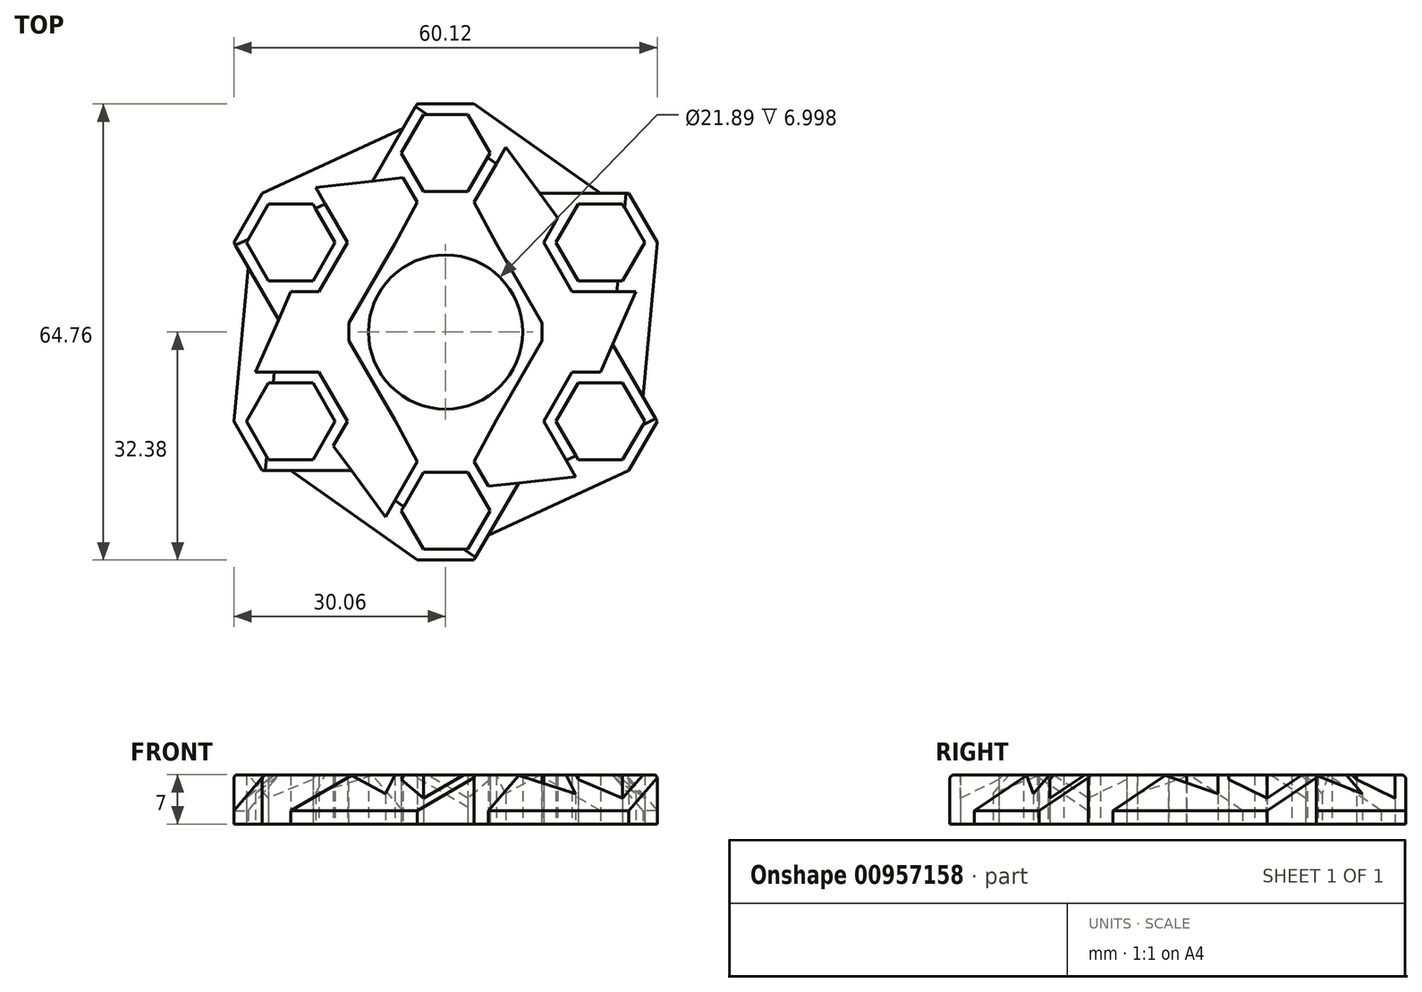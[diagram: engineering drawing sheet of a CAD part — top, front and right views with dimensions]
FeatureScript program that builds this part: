
annotation { "Feature Type Name" : "Feature", "Feature Type Description" : "" }
export const myFeature = defineFeature(function(context is Context, id is Id, definition is map)
    precondition{}
    {
        {
            var Q0;
            Q0=qCreatedBy(makeId("Top.planeOp"),FACE);
            var sketch = newSketch(context, id + "F0", { "sketchPlane" : qUnion([Q0])});
            skCircle(sketch, "E0", {"center": v(0, 0) * mm, "radius": 10.95 * mm});
            skCircle(sketch, "E1.cCircle", {"center": v(0, 0) * mm, "radius": 12.5 * mm, "construction": true});
            skLineSegment(sketch, "E1.0", {"start": v(-7.22, 12.5) * mm, "end": v(7.22, 12.5) * mm});
            skLineSegment(sketch, "E1.1", {"start": v(7.22, 12.5) * mm, "end": v(14.44, 0) * mm});
            skLineSegment(sketch, "E1.2", {"start": v(14.44, 0) * mm, "end": v(7.22, -12.5) * mm});
            skLineSegment(sketch, "E1.3", {"start": v(7.22, -12.5) * mm, "end": v(-7.22, -12.5) * mm});
            skLineSegment(sketch, "E1.4", {"start": v(-7.22, -12.5) * mm, "end": v(-14.44, 0) * mm});
            skLineSegment(sketch, "E1.5", {"start": v(-14.44, 0) * mm, "end": v(-7.22, 12.5) * mm});
            skPoint(sketch, "E1.0.midPoint", {"position": v(0, 12.5) * mm});
            skLineSegment(sketch, "E2", {"start": v(0, 0) * mm, "end": v(-2.16, 1.25) * mm});
            skLineSegment(sketch, "E3", {"start": v(0, 0) * mm, "end": v(22, -12.7) * mm});
            skLineSegment(sketch, "E4", {"start": v(22, -12.7) * mm, "end": v(-22, 12.7) * mm});
            skLineSegment(sketch, "E5", {"start": v(0, 0) * mm, "end": v(-22, -12.7) * mm});
            skLineSegment(sketch, "E6", {"start": v(0, 0) * mm, "end": v(22, 12.7) * mm});
            skCircle(sketch, "E7.cCircle", {"center": v(0, 25.4) * mm, "radius": 6.99 * mm, "construction": true});
            skLineSegment(sketch, "E7.0", {"start": v(4.03, 18.41) * mm, "end": v(-4.03, 18.41) * mm});
            skLineSegment(sketch, "E7.1", {"start": v(-4.03, 18.42) * mm, "end": v(-8.07, 25.4) * mm});
            skLineSegment(sketch, "E7.2", {"start": v(-8.07, 25.4) * mm, "end": v(-4.03, 32.39) * mm});
            skLineSegment(sketch, "E7.3", {"start": v(-4.03, 32.38) * mm, "end": v(4.03, 32.38) * mm});
            skLineSegment(sketch, "E7.4", {"start": v(4.03, 32.39) * mm, "end": v(8.07, 25.4) * mm});
            skLineSegment(sketch, "E7.5", {"start": v(8.07, 25.4) * mm, "end": v(4.03, 18.42) * mm});
            skPoint(sketch, "E7.0.midPoint", {"position": v(0, 18.41) * mm});
            skCircle(sketch, "E8.cCircle", {"center": v(22, 12.7) * mm, "radius": 6.98 * mm, "construction": true});
            skLineSegment(sketch, "E8.0", {"start": v(17.96, 5.71) * mm, "end": v(13.93, 12.7) * mm});
            skLineSegment(sketch, "E8.1", {"start": v(13.93, 12.7) * mm, "end": v(17.96, 19.68) * mm});
            skLineSegment(sketch, "E8.2", {"start": v(17.96, 19.68) * mm, "end": v(26.03, 19.69) * mm});
            skLineSegment(sketch, "E8.3", {"start": v(26.03, 19.69) * mm, "end": v(30.06, 12.7) * mm});
            skLineSegment(sketch, "E8.4", {"start": v(30.06, 12.7) * mm, "end": v(26.03, 5.71) * mm});
            skLineSegment(sketch, "E8.5", {"start": v(26.03, 5.71) * mm, "end": v(17.96, 5.71) * mm});
            skPoint(sketch, "E8.0.midPoint", {"position": v(15.95, 9.2) * mm});
            skCircle(sketch, "E9.cCircle", {"center": v(-22, 12.7) * mm, "radius": 6.99 * mm, "construction": true});
            skLineSegment(sketch, "E9.0", {"start": v(-13.93, 12.7) * mm, "end": v(-17.96, 5.72) * mm});
            skLineSegment(sketch, "E9.1", {"start": v(-17.96, 5.72) * mm, "end": v(-26.03, 5.71) * mm});
            skLineSegment(sketch, "E9.2", {"start": v(-26.03, 5.71) * mm, "end": v(-30.06, 12.7) * mm});
            skLineSegment(sketch, "E9.3", {"start": v(-30.06, 12.7) * mm, "end": v(-26.03, 19.68) * mm});
            skLineSegment(sketch, "E9.4", {"start": v(-26.03, 19.68) * mm, "end": v(-17.96, 19.68) * mm});
            skLineSegment(sketch, "E9.5", {"start": v(-17.96, 19.69) * mm, "end": v(-13.93, 12.7) * mm});
            skPoint(sketch, "E9.0.midPoint", {"position": v(-15.95, 9.2) * mm});
            skCircle(sketch, "E10.cCircle", {"center": v(-22, -12.7) * mm, "radius": 6.98 * mm, "construction": true});
            skLineSegment(sketch, "E10.0", {"start": v(-17.96, -5.71) * mm, "end": v(-13.93, -12.7) * mm});
            skLineSegment(sketch, "E10.1", {"start": v(-13.93, -12.7) * mm, "end": v(-17.96, -19.69) * mm});
            skLineSegment(sketch, "E10.2", {"start": v(-17.96, -19.69) * mm, "end": v(-26.03, -19.69) * mm});
            skLineSegment(sketch, "E10.3", {"start": v(-26.03, -19.69) * mm, "end": v(-30.06, -12.7) * mm});
            skLineSegment(sketch, "E10.4", {"start": v(-30.06, -12.7) * mm, "end": v(-26.03, -5.71) * mm});
            skLineSegment(sketch, "E10.5", {"start": v(-26.03, -5.71) * mm, "end": v(-17.96, -5.72) * mm});
            skPoint(sketch, "E10.0.midPoint", {"position": v(-15.95, -9.2) * mm});
            skCircle(sketch, "E11.cCircle", {"center": v(22, -12.7) * mm, "radius": 6.98 * mm, "construction": true});
            skLineSegment(sketch, "E11.0", {"start": v(13.93, -12.7) * mm, "end": v(17.96, -5.72) * mm});
            skLineSegment(sketch, "E11.1", {"start": v(17.96, -5.72) * mm, "end": v(26.03, -5.72) * mm});
            skLineSegment(sketch, "E11.2", {"start": v(26.03, -5.71) * mm, "end": v(30.06, -12.7) * mm});
            skLineSegment(sketch, "E11.3", {"start": v(30.06, -12.7) * mm, "end": v(26.03, -19.69) * mm});
            skLineSegment(sketch, "E11.4", {"start": v(26.03, -19.68) * mm, "end": v(17.96, -19.69) * mm});
            skLineSegment(sketch, "E11.5", {"start": v(17.96, -19.69) * mm, "end": v(13.93, -12.7) * mm});
            skPoint(sketch, "E11.0.midPoint", {"position": v(15.95, -9.2) * mm});
            skCircle(sketch, "E12.cCircle", {"center": v(0, -25.4) * mm, "radius": 6.99 * mm, "construction": true});
            skLineSegment(sketch, "E12.0", {"start": v(-4.03, -18.41) * mm, "end": v(4.03, -18.41) * mm});
            skLineSegment(sketch, "E12.1", {"start": v(4.03, -18.42) * mm, "end": v(8.07, -25.4) * mm});
            skLineSegment(sketch, "E12.2", {"start": v(8.07, -25.4) * mm, "end": v(4.03, -32.38) * mm});
            skLineSegment(sketch, "E12.3", {"start": v(4.03, -32.39) * mm, "end": v(-4.03, -32.39) * mm});
            skLineSegment(sketch, "E12.4", {"start": v(-4.03, -32.39) * mm, "end": v(-8.07, -25.4) * mm});
            skLineSegment(sketch, "E12.5", {"start": v(-8.07, -25.4) * mm, "end": v(-4.03, -18.41) * mm});
            skPoint(sketch, "E12.0.midPoint", {"position": v(0, -18.41) * mm});
            skCircle(sketch, "E13.cCircle", {"center": v(0, 25.4) * mm, "radius": 5.46 * mm, "construction": true});
            skLineSegment(sketch, "E13.0", {"start": v(-3.15, 30.86) * mm, "end": v(3.15, 30.86) * mm});
            skLineSegment(sketch, "E13.1", {"start": v(3.15, 30.86) * mm, "end": v(6.3, 25.4) * mm});
            skLineSegment(sketch, "E13.2", {"start": v(6.3, 25.4) * mm, "end": v(3.15, 19.94) * mm});
            skLineSegment(sketch, "E13.3", {"start": v(3.15, 19.94) * mm, "end": v(-3.15, 19.94) * mm});
            skLineSegment(sketch, "E13.4", {"start": v(-3.15, 19.94) * mm, "end": v(-6.3, 25.4) * mm});
            skLineSegment(sketch, "E13.5", {"start": v(-6.3, 25.4) * mm, "end": v(-3.15, 30.86) * mm});
            skPoint(sketch, "E13.0.midPoint", {"position": v(0, 30.86) * mm});
            skCircle(sketch, "E14.cCircle", {"center": v(22, 12.7) * mm, "radius": 5.46 * mm, "construction": true});
            skLineSegment(sketch, "E14.0", {"start": v(18.84, 7.24) * mm, "end": v(15.7, 12.7) * mm});
            skLineSegment(sketch, "E14.1", {"start": v(15.7, 12.7) * mm, "end": v(18.84, 18.16) * mm});
            skLineSegment(sketch, "E14.2", {"start": v(18.84, 18.16) * mm, "end": v(25.15, 18.16) * mm});
            skLineSegment(sketch, "E14.3", {"start": v(25.15, 18.16) * mm, "end": v(28.3, 12.7) * mm});
            skLineSegment(sketch, "E14.4", {"start": v(28.3, 12.7) * mm, "end": v(25.15, 7.24) * mm});
            skLineSegment(sketch, "E14.5", {"start": v(25.15, 7.24) * mm, "end": v(18.84, 7.24) * mm});
            skPoint(sketch, "E14.0.midPoint", {"position": v(17.27, 9.97) * mm});
            skCircle(sketch, "E15.cCircle", {"center": v(22, -12.7) * mm, "radius": 5.46 * mm, "construction": true});
            skLineSegment(sketch, "E15.0", {"start": v(15.7, -12.7) * mm, "end": v(18.84, -7.24) * mm});
            skLineSegment(sketch, "E15.1", {"start": v(18.84, -7.24) * mm, "end": v(25.15, -7.24) * mm});
            skLineSegment(sketch, "E15.2", {"start": v(25.15, -7.24) * mm, "end": v(28.3, -12.7) * mm});
            skLineSegment(sketch, "E15.3", {"start": v(28.3, -12.7) * mm, "end": v(25.15, -18.16) * mm});
            skLineSegment(sketch, "E15.4", {"start": v(25.15, -18.16) * mm, "end": v(18.84, -18.16) * mm});
            skLineSegment(sketch, "E15.5", {"start": v(18.84, -18.16) * mm, "end": v(15.7, -12.7) * mm});
            skPoint(sketch, "E15.0.midPoint", {"position": v(17.27, -9.97) * mm});
            skCircle(sketch, "E16.cCircle", {"center": v(0, -25.4) * mm, "radius": 5.46 * mm, "construction": true});
            skLineSegment(sketch, "E16.0", {"start": v(-3.15, -19.94) * mm, "end": v(3.15, -19.94) * mm});
            skLineSegment(sketch, "E16.1", {"start": v(3.15, -19.94) * mm, "end": v(6.3, -25.4) * mm});
            skLineSegment(sketch, "E16.2", {"start": v(6.3, -25.4) * mm, "end": v(3.15, -30.86) * mm});
            skLineSegment(sketch, "E16.3", {"start": v(3.15, -30.86) * mm, "end": v(-3.15, -30.86) * mm});
            skLineSegment(sketch, "E16.4", {"start": v(-3.15, -30.86) * mm, "end": v(-6.3, -25.4) * mm});
            skLineSegment(sketch, "E16.5", {"start": v(-6.3, -25.4) * mm, "end": v(-3.15, -19.94) * mm});
            skPoint(sketch, "E16.0.midPoint", {"position": v(0, -19.94) * mm});
            skCircle(sketch, "E17.cCircle", {"center": v(-22, -12.7) * mm, "radius": 5.46 * mm, "construction": true});
            skLineSegment(sketch, "E17.0", {"start": v(-18.84, -7.24) * mm, "end": v(-15.7, -12.7) * mm});
            skLineSegment(sketch, "E17.1", {"start": v(-15.7, -12.7) * mm, "end": v(-18.84, -18.16) * mm});
            skLineSegment(sketch, "E17.2", {"start": v(-18.84, -18.16) * mm, "end": v(-25.15, -18.16) * mm});
            skLineSegment(sketch, "E17.3", {"start": v(-25.15, -18.16) * mm, "end": v(-28.3, -12.7) * mm});
            skLineSegment(sketch, "E17.4", {"start": v(-28.3, -12.7) * mm, "end": v(-25.15, -7.24) * mm});
            skLineSegment(sketch, "E17.5", {"start": v(-25.15, -7.24) * mm, "end": v(-18.84, -7.24) * mm});
            skPoint(sketch, "E17.0.midPoint", {"position": v(-17.27, -9.97) * mm});
            skCircle(sketch, "E18.cCircle", {"center": v(-22, 12.7) * mm, "radius": 5.46 * mm, "construction": true});
            skLineSegment(sketch, "E18.0", {"start": v(-15.7, 12.7) * mm, "end": v(-18.84, 7.24) * mm});
            skLineSegment(sketch, "E18.1", {"start": v(-18.84, 7.24) * mm, "end": v(-25.15, 7.24) * mm});
            skLineSegment(sketch, "E18.2", {"start": v(-25.15, 7.24) * mm, "end": v(-28.3, 12.7) * mm});
            skLineSegment(sketch, "E18.3", {"start": v(-28.3, 12.7) * mm, "end": v(-25.15, 18.16) * mm});
            skLineSegment(sketch, "E18.4", {"start": v(-25.15, 18.16) * mm, "end": v(-18.84, 18.16) * mm});
            skLineSegment(sketch, "E18.5", {"start": v(-18.84, 18.16) * mm, "end": v(-15.7, 12.7) * mm});
            skPoint(sketch, "E18.0.midPoint", {"position": v(-17.27, 9.97) * mm});
            skLineSegment(sketch, "E19", {"start": v(-30.06, -12.7) * mm, "end": v(-22, 5.72) * mm});
            skLineSegment(sketch, "E20", {"start": v(4.03, 32.39) * mm, "end": v(15.95, 16.2) * mm});
            skLineSegment(sketch, "E21", {"start": v(26.03, -19.69) * mm, "end": v(6.05, -21.9) * mm});
            skLineSegment(sketch, "E22", {"start": v(-15.95, -16.2) * mm, "end": v(-4.03, -32.39) * mm});
            skLineSegment(sketch, "E23", {"start": v(22, -5.72) * mm, "end": v(30.06, 12.7) * mm});
            skLineSegment(sketch, "E24", {"start": v(-26.03, 19.68) * mm, "end": v(-6.05, 21.9) * mm});
            skLineSegment(sketch, "E25", {"start": v(-26.03, -5.71) * mm, "end": v(-27, -5.71) * mm});
            skLineSegment(sketch, "E26", {"start": v(-17.96, 19.68) * mm, "end": v(-18.45, 20.53) * mm});
            skLineSegment(sketch, "E27", {"start": v(26.03, 5.71) * mm, "end": v(27, 5.71) * mm});
            skLineSegment(sketch, "E28", {"start": v(17.96, -19.69) * mm, "end": v(18.45, -20.53) * mm});
            skLineSegment(sketch, "E29", {"start": v(-4.03, 18.41) * mm, "end": v(-7.22, 12.5) * mm});
            skLineSegment(sketch, "E30", {"start": v(4.03, 18.42) * mm, "end": v(7.22, 12.5) * mm});
            skLineSegment(sketch, "E31", {"start": v(7.22, -12.5) * mm, "end": v(4.03, -18.41) * mm});
            skLineSegment(sketch, "E32", {"start": v(-7.22, -12.5) * mm, "end": v(-4.03, -18.41) * mm});
            skLineSegment(sketch, "E33", {"start": v(-28.05, 9.2) * mm, "end": v(-30.06, -12.7) * mm});
            skLineSegment(sketch, "E34", {"start": v(-6.05, 28.9) * mm, "end": v(-26.03, 19.68) * mm});
            skLineSegment(sketch, "E35", {"start": v(28.05, -9.2) * mm, "end": v(30.06, 12.7) * mm});
            skPoint(sketch, "E35.startSnap0", {"position": v(28.05, -9.2) * mm});
            skLineSegment(sketch, "E36", {"start": v(6.05, -28.9) * mm, "end": v(26.03, -19.69) * mm});
            skPoint(sketch, "E36.startSnap0", {"position": v(6.05, -28.9) * mm});
            skLineSegment(sketch, "E37", {"start": v(-22, -19.69) * mm, "end": v(-4.03, -32.39) * mm});
            skLineSegment(sketch, "E38", {"start": v(22, 19.69) * mm, "end": v(4.03, 32.39) * mm});
            skLineSegment(sketch, "E39", {"start": v(8.07, 25.4) * mm, "end": v(8.55, 26.24) * mm});
            skLineSegment(sketch, "E40", {"start": v(-8.07, -25.4) * mm, "end": v(-8.55, -26.24) * mm});
            skSolve(sketch);
        }
        {
            var Q0;
            {var subQ1=sQuery(id+"F0.wireOp",EDGE,"a8906091-ae58-46a8-9056-1b7c50979c71.1");Q0=makeQuery(id+"F0.imprint","IMPRINT",FACE,{"disambiguationData":[TD([[makeQuery(id+"F0.imprint","IMPRINT",EDGE,{"derivedFrom":subQ1}),-1.0]])]});}
            var Q1;
            Q1=makeQuery(id+"F0.imprint","IMPRINT",FACE,{"disambiguationData":[TD([[makeQuery(id+"F0.imprint","IMPRINT",EDGE,{"derivedFrom":sQuery(id+"F0.wireOp",EDGE,"d1o7id8u-C8pC-OSs5-cJyL-PHeGcIzq2Z2Q")}),-1.0]])]});
            var Q2;
            {var subQ1=sQuery(id+"F0.wireOp",EDGE,"fe929a84-09fa-4d52-ac2d-c80ecc7f6bf3.1");Q2=makeQuery(id+"F0.imprint","IMPRINT",FACE,{"disambiguationData":[TD([[makeQuery(id+"F0.imprint","IMPRINT",EDGE,{"derivedFrom":subQ1}),-1.0]])]});}
            var Q3;
            {var subQ1=sQuery(id+"F0.wireOp",EDGE,"61db4338-95e5-4235-af2c-2ea44c3c3e1a.1");Q3=makeQuery(id+"F0.imprint","IMPRINT",FACE,{"disambiguationData":[TD([[makeQuery(id+"F0.imprint","IMPRINT",EDGE,{"derivedFrom":subQ1}),-1.0]])]});}
            var Q4;
            Q4=makeQuery(id+"F0.imprint","IMPRINT",FACE,{"disambiguationData":[TD([[makeQuery(id+"F0.imprint","IMPRINT",EDGE,{"derivedFrom":sQuery(id+"F0.wireOp",EDGE,"9b93c930-f82c-4a72-9d49-0b687060dcdc.0")}),1.0]])]});
            var Q5;
            {var subQ2=sQuery(id+"F0.wireOp",EDGE,"a4857317-28d0-40ab-9de1-f5b2b211004c.1");Q5=makeQuery(id+"F0.imprint","IMPRINT",FACE,{"disambiguationData":[TD([[makeQuery(id+"F0.imprint","IMPRINT",EDGE,{"derivedFrom":subQ2}),-1.0]])]});}
            var Q6;
            {var subQ4=sQuery(id+"F0.wireOp",EDGE,"b6a689d3-a215-44eb-954f-cb7c50705edb.1");Q6=makeQuery(id+"F0.imprint","IMPRINT",FACE,{"disambiguationData":[TD([[makeQuery(id+"F0.imprint","IMPRINT",EDGE,{"derivedFrom":subQ4}),-1.0]])]});}
            var Q7;
            {var subQ1=sQuery(id+"F0.wireOp",EDGE,"a8906091-ae58-46a8-9056-1b7c50979c71.1");Q7=makeQuery(id+"F0.imprint","IMPRINT",FACE,{"disambiguationData":[TD([[makeQuery(id+"F0.imprint","IMPRINT",EDGE,{"derivedFrom":subQ1}),1.0]])]});}
            var Q8;
            Q8=makeQuery(id+"F0.imprint","IMPRINT",FACE,{"disambiguationData":[TD([[makeQuery(id+"F0.imprint","IMPRINT",EDGE,{"derivedFrom":sQuery(id+"F0.wireOp",EDGE,"fe929a84-09fa-4d52-ac2d-c80ecc7f6bf3.3")}),1.0]])]});
            var Q9;
            Q9=makeQuery(id+"F0.imprint","IMPRINT",FACE,{"disambiguationData":[TD([[makeQuery(id+"F0.imprint","IMPRINT",EDGE,{"derivedFrom":sQuery(id+"F0.wireOp",EDGE,"a8906091-ae58-46a8-9056-1b7c50979c71.3")}),1.0]])]});
            var Q10;
            {var subQ4=sQuery(id+"F0.wireOp",EDGE,"a8906091-ae58-46a8-9056-1b7c50979c71.5");Q10=makeQuery(id+"F0.imprint","IMPRINT",FACE,{"disambiguationData":[TD([[makeQuery(id+"F0.imprint","IMPRINT",EDGE,{"derivedFrom":subQ4}),1.0]])]});}
            var Q11;
            Q11=makeQuery(id+"F0.imprint","IMPRINT",FACE,{"disambiguationData":[TD([[makeQuery(id+"F0.imprint","IMPRINT",EDGE,{"derivedFrom":sQuery(id+"F0.wireOp",EDGE,"14990129-b4ae-4c4f-9826-e155054ce366.3")}),1.0]])]});
            var Q12;
            {var subQ4=sQuery(id+"F0.wireOp",EDGE,"a4857317-28d0-40ab-9de1-f5b2b211004c.1");Q12=makeQuery(id+"F0.imprint","IMPRINT",FACE,{"disambiguationData":[TD([[makeQuery(id+"F0.imprint","IMPRINT",EDGE,{"derivedFrom":subQ4}),1.0]])]});}
            var Q13;
            Q13=makeQuery(id+"F0.imprint","IMPRINT",FACE,{"disambiguationData":[TD([[makeQuery(id+"F0.imprint","IMPRINT",EDGE,{"derivedFrom":sQuery(id+"F0.wireOp",EDGE,"a4857317-28d0-40ab-9de1-f5b2b211004c.3")}),1.0]])]});
            var Q14;
            {var subQ1=sQuery(id+"F0.wireOp",EDGE,"b6a689d3-a215-44eb-954f-cb7c50705edb.1");Q14=makeQuery(id+"F0.imprint","IMPRINT",FACE,{"disambiguationData":[TD([[makeQuery(id+"F0.imprint","IMPRINT",EDGE,{"derivedFrom":subQ1}),1.0]])]});}
            var Q15;
            Q15=makeQuery(id+"F0.imprint","IMPRINT",FACE,{"disambiguationData":[TD([[makeQuery(id+"F0.imprint","IMPRINT",EDGE,{"derivedFrom":sQuery(id+"F0.wireOp",EDGE,"b6a689d3-a215-44eb-954f-cb7c50705edb.3")}),1.0]])]});
            var Q16;
            {var subQ1=sQuery(id+"F0.wireOp",EDGE,"fe929a84-09fa-4d52-ac2d-c80ecc7f6bf3.1");Q16=makeQuery(id+"F0.imprint","IMPRINT",FACE,{"disambiguationData":[TD([[makeQuery(id+"F0.imprint","IMPRINT",EDGE,{"derivedFrom":subQ1}),1.0]])]});}
            var Q17;
            Q17=makeQuery(id+"F0.imprint","IMPRINT",FACE,{"disambiguationData":[TD([[makeQuery(id+"F0.imprint","IMPRINT",EDGE,{"derivedFrom":sQuery(id+"F0.wireOp",EDGE,"61db4338-95e5-4235-af2c-2ea44c3c3e1a.3")}),1.0]])]});
            var Q18;
            {var subQ2=sQuery(id+"F0.wireOp",EDGE,"61db4338-95e5-4235-af2c-2ea44c3c3e1a.5");Q18=makeQuery(id+"F0.imprint","IMPRINT",FACE,{"disambiguationData":[TD([[makeQuery(id+"F0.imprint","IMPRINT",EDGE,{"derivedFrom":subQ2}),1.0]])]});}
            var Q19;
            Q19=makeQuery(id+"F0.imprint","IMPRINT",FACE,{"disambiguationData":[TD([[makeQuery(id+"F0.imprint","IMPRINT",EDGE,{"derivedFrom":sQuery(id+"F0.wireOp",EDGE,"a8906091-ae58-46a8-9056-1b7c50979c71.2")}),-1.0]])]});
            var Q20;
            {var subQ4=sQuery(id+"F0.wireOp",EDGE,"E10.2");Q20=makeQuery(id+"F0.imprint","IMPRINT",FACE,{"disambiguationData":[TD([[makeQuery(id+"F0.imprint","IMPRINT",EDGE,{"derivedFrom":subQ4}),-1.0]])]});}
            var Q21;
            {var subQ0=sQuery(id+"F0.wireOp",EDGE,"E4");var subQ1=sQuery(id+"F0.wireOp",EDGE,"E0");var subQ2=makeQuery(id+"F0.imprint","INTERSECT",VERTEX,{"disambiguationData":[OD(0.0)],"derivedFrom":[subQ1,subQ0]});Q21=makeQuery(id+"F0.imprint","IMPRINT",FACE,{"disambiguationData":[TD([[makeQuery(id+"F0.imprint","IMPRINT",EDGE,{"disambiguationData":[TD([[subQ2,-1.0]])],"derivedFrom":subQ1}),-1.0]])]});}
            var Q22;
            {var subQ5=sQuery(id+"F0.wireOp",EDGE,"E9.2");Q22=makeQuery(id+"F0.imprint","IMPRINT",FACE,{"disambiguationData":[TD([[makeQuery(id+"F0.imprint","IMPRINT",EDGE,{"derivedFrom":subQ5}),-1.0]])]});}
            var Q23;
            {var subQ0=sQuery(id+"F0.wireOp",EDGE,"E9.2");Q23=makeQuery(id+"F0.imprint","IMPRINT",FACE,{"disambiguationData":[TD([[makeQuery(id+"F0.imprint","IMPRINT",EDGE,{"derivedFrom":subQ0}),1.0]])]});}
            var Q24;
            {var subQ0=sQuery(id+"F0.wireOp",EDGE,"E7.2");Q24=makeQuery(id+"F0.imprint","IMPRINT",FACE,{"disambiguationData":[TD([[makeQuery(id+"F0.imprint","IMPRINT",EDGE,{"derivedFrom":subQ0}),1.0]])]});}
            var Q25;
            {var subQ3=sQuery(id+"F0.wireOp",EDGE,"E7.0");Q25=makeQuery(id+"F0.imprint","IMPRINT",FACE,{"disambiguationData":[TD([[makeQuery(id+"F0.imprint","IMPRINT",EDGE,{"derivedFrom":subQ3}),-1.0]])]});}
            var Q26;
            {var subQ0=sQuery(id+"F0.wireOp",EDGE,"E8.2");Q26=makeQuery(id+"F0.imprint","IMPRINT",FACE,{"disambiguationData":[TD([[makeQuery(id+"F0.imprint","IMPRINT",EDGE,{"derivedFrom":subQ0}),1.0]])]});}
            var Q27;
            {var subQ0=sQuery(id+"F0.wireOp",EDGE,"E11.2");Q27=makeQuery(id+"F0.imprint","IMPRINT",FACE,{"disambiguationData":[TD([[makeQuery(id+"F0.imprint","IMPRINT",EDGE,{"derivedFrom":subQ0}),1.0]])]});}
            var Q28;
            {var subQ2=sQuery(id+"F0.wireOp",EDGE,"E8.2");Q28=makeQuery(id+"F0.imprint","IMPRINT",FACE,{"disambiguationData":[TD([[makeQuery(id+"F0.imprint","IMPRINT",EDGE,{"derivedFrom":subQ2}),-1.0]])]});}
            var Q29;
            {var subQ0=sQuery(id+"F0.wireOp",EDGE,"E12.2");Q29=makeQuery(id+"F0.imprint","IMPRINT",FACE,{"disambiguationData":[TD([[makeQuery(id+"F0.imprint","IMPRINT",EDGE,{"derivedFrom":subQ0}),1.0]])]});}
            var Q30;
            {var subQ0=sQuery(id+"F0.wireOp",EDGE,"E12.0");Q30=makeQuery(id+"F0.imprint","IMPRINT",FACE,{"disambiguationData":[TD([[makeQuery(id+"F0.imprint","IMPRINT",EDGE,{"derivedFrom":subQ0}),-1.0]])]});}
            var Q31;
            {var subQ0=sQuery(id+"F0.wireOp",EDGE,"E10.2");Q31=makeQuery(id+"F0.imprint","IMPRINT",FACE,{"disambiguationData":[TD([[makeQuery(id+"F0.imprint","IMPRINT",EDGE,{"derivedFrom":subQ0}),1.0]])]});}
            var Q32;
            {var subQ1=sQuery(id+"F0.wireOp",EDGE,"E1.3");Q32=makeQuery(id+"F0.imprint","IMPRINT",FACE,{"disambiguationData":[TD([[makeQuery(id+"F0.imprint","IMPRINT",EDGE,{"derivedFrom":subQ1}),-1.0]])]});}
            var Q33;
            {var subQ1=sQuery(id+"F0.wireOp",EDGE,"E0");var subQ7=sQuery(id+"F0.wireOp",EDGE,"E6");var subQ9=makeQuery(id+"F0.imprint","INTERSECT",VERTEX,{"derivedFrom":[subQ1,subQ7]});Q33=makeQuery(id+"F0.imprint","IMPRINT",FACE,{"disambiguationData":[TD([[makeQuery(id+"F0.imprint","IMPRINT",EDGE,{"disambiguationData":[TD([[subQ9,1.0]])],"derivedFrom":subQ1}),-1.0]])]});}
            var Q34;
            {var subQ1=sQuery(id+"F0.wireOp",EDGE,"E1.0");Q34=makeQuery(id+"F0.imprint","IMPRINT",FACE,{"disambiguationData":[TD([[makeQuery(id+"F0.imprint","IMPRINT",EDGE,{"derivedFrom":subQ1}),-1.0]])]});}
            var Q35;
            {var subQ5=sQuery(id+"F0.wireOp",EDGE,"E11.2");Q35=makeQuery(id+"F0.imprint","IMPRINT",FACE,{"disambiguationData":[TD([[makeQuery(id+"F0.imprint","IMPRINT",EDGE,{"derivedFrom":subQ5}),-1.0]])]});}
            var Q36;
            {var subQ0=sQuery(id+"F0.wireOp",EDGE,"E9.4");Q36=makeQuery(id+"F0.imprint","IMPRINT",FACE,{"disambiguationData":[TD([[makeQuery(id+"F0.imprint","IMPRINT",EDGE,{"derivedFrom":subQ0}),1.0]])]});}
            var Q37;
            {var subQ0=sQuery(id+"F0.wireOp",EDGE,"E8.4");Q37=makeQuery(id+"F0.imprint","IMPRINT",FACE,{"disambiguationData":[TD([[makeQuery(id+"F0.imprint","IMPRINT",EDGE,{"derivedFrom":subQ0}),1.0]])]});}
            var Q38;
            {var subQ0=sQuery(id+"F0.wireOp",EDGE,"E11.4");Q38=makeQuery(id+"F0.imprint","IMPRINT",FACE,{"disambiguationData":[TD([[makeQuery(id+"F0.imprint","IMPRINT",EDGE,{"derivedFrom":subQ0}),1.0]])]});}
            var Q39;
            {var subQ0=sQuery(id+"F0.wireOp",EDGE,"E10.4");Q39=makeQuery(id+"F0.imprint","IMPRINT",FACE,{"disambiguationData":[TD([[makeQuery(id+"F0.imprint","IMPRINT",EDGE,{"derivedFrom":subQ0}),1.0]])]});}
            var Q40;
            Q40=makeQuery(id+"F0.imprint","IMPRINT",FACE,{"disambiguationData":[TD([[makeQuery(id+"F0.imprint","IMPRINT",EDGE,{"derivedFrom":sQuery(id+"F0.wireOp",EDGE,"E1.0")}),1.0]])]});
            var Q41;
            Q41=makeQuery(id+"F0.imprint","IMPRINT",FACE,{"disambiguationData":[TD([[makeQuery(id+"F0.imprint","IMPRINT",EDGE,{"derivedFrom":sQuery(id+"F0.wireOp",EDGE,"E1.3")}),1.0]])]});
            var Q42;
            {var subQ0=sQuery(id+"F0.wireOp",EDGE,"E12.4");Q42=makeQuery(id+"F0.imprint","IMPRINT",FACE,{"disambiguationData":[TD([[makeQuery(id+"F0.imprint","IMPRINT",EDGE,{"derivedFrom":subQ0}),1.0]])]});}
            var Q43;
            {var subQ0=sQuery(id+"F0.wireOp",EDGE,"E7.4");Q43=makeQuery(id+"F0.imprint","IMPRINT",FACE,{"disambiguationData":[TD([[makeQuery(id+"F0.imprint","IMPRINT",EDGE,{"derivedFrom":subQ0}),1.0]])]});}
            extrude(context, id + "F1", {"entities" : qUnion([Q0, Q1, Q2, Q3, Q4, Q5, Q6, Q7, Q8, Q9, Q10, Q11, Q12, Q13, Q14, Q15, Q16, Q17, Q18, Q19, Q20, Q21, Q22, Q23, Q24, Q25, Q26, Q27, Q28, Q29, Q30, Q31, Q32, Q33, Q34, Q35, Q36, Q37, Q38, Q39, Q40, Q41, Q42, Q43]), "depth" : 7 * mm, "offsetDistance" : 25.4 * mm});
        }
        {
            var Q0;
            Q0=makeQuery(id+"F1.opExtrude","CAP_EDGE",EDGE,{"disambiguationData":[OSD([sQuery(id+"F0.wireOp",EDGE,"E35")])],"isStart":false});
            var Q1;
            Q1=makeQuery(id+"F1.opExtrude","CAP_EDGE",EDGE,{"disambiguationData":[OSD([sQuery(id+"F0.wireOp",EDGE,"E38")])],"isStart":false});
            var Q2;
            Q2=makeQuery(id+"F1.opExtrude","CAP_EDGE",EDGE,{"disambiguationData":[OSD([sQuery(id+"F0.wireOp",EDGE,"E34")])],"isStart":false});
            var Q3;
            Q3=makeQuery(id+"F1.opExtrude","CAP_EDGE",EDGE,{"disambiguationData":[OSD([sQuery(id+"F0.wireOp",EDGE,"E33")])],"isStart":false});
            var Q4;
            Q4=makeQuery(id+"F1.opExtrude","CAP_EDGE",EDGE,{"disambiguationData":[OSD([sQuery(id+"F0.wireOp",EDGE,"E37")])],"isStart":false});
            var Q5;
            Q5=makeQuery(id+"F1.opExtrude","CAP_EDGE",EDGE,{"disambiguationData":[OSD([sQuery(id+"F0.wireOp",EDGE,"E36")])],"isStart":false});
            chamfer(context, id + "F2", {"entities" : qUnion([Q0, Q1, Q2, Q3, Q4, Q5]), "width" : 5.08 * mm, "tangentPropagation" : true});
        }
        {
            var Q0;
            Q0=makeQuery(id+"F1.opExtrude","SWEPT_EDGE",EDGE,{"disambiguationData":[OSD([sQuery(id+"F0.wireOp",EDGE,"E1.4"),sQuery(id+"F0.wireOp",EDGE,"E1.5")])]});
            var Q1;
            Q1=makeQuery(id+"F1.opExtrude","SWEPT_EDGE",EDGE,{"disambiguationData":[OSD([sQuery(id+"F0.wireOp",EDGE,"E1.1"),sQuery(id+"F0.wireOp",EDGE,"E1.2")])]});
            chamfer(context, id + "F3", {"entities" : qUnion([Q0, Q1]), "width" : 2.54 * mm, "tangentPropagation" : true});
        }
    });
